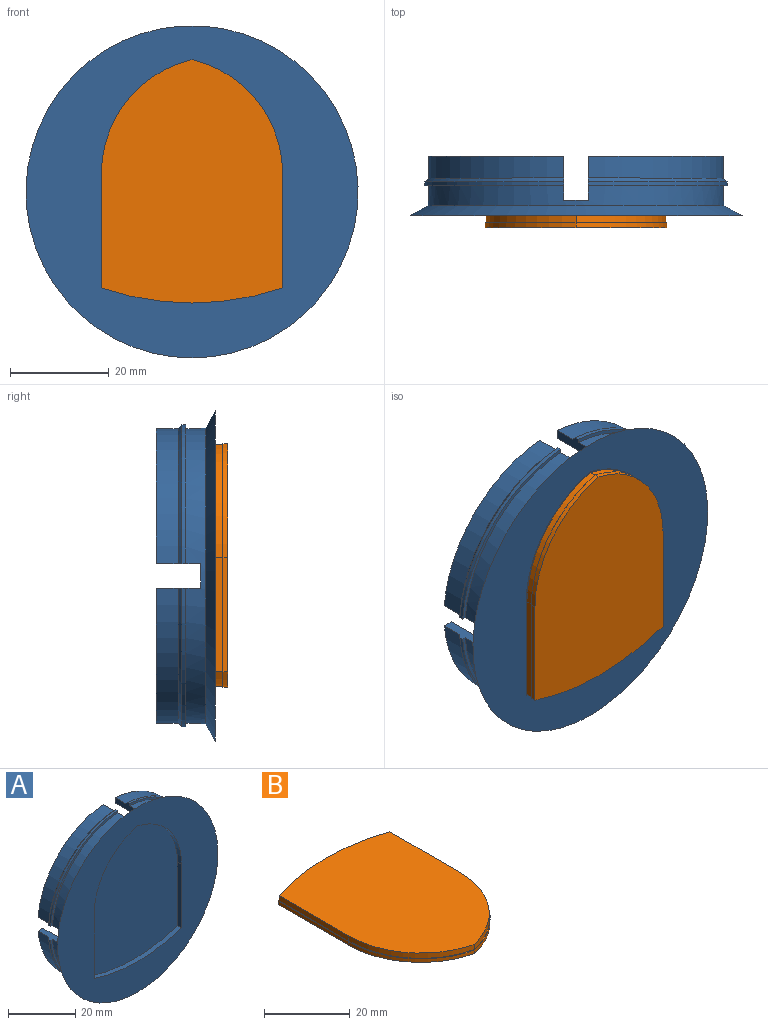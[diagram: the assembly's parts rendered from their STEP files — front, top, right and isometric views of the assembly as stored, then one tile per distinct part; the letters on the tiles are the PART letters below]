
ASSEMBLY  parts=2 mates=1
PART A: 42 faces, bbox 67.4x12x67.4 mm
  f0: plane 67.4x67.4mm, normal (0,-1,0), area 2005.3mm2, adj f35,f36,f37,f38,f39,f40
  f1: cylinder r=28mm len=25.39mm, axis (0,-1,0), area 350.8mm2, adj f12,f29,f31,f34
  f2: cylinder r=28mm len=25.39mm, axis (0,-1,0), area 350.8mm2, adj f14,f26,f28,f34
  f3: cylinder r=28mm len=25.39mm, axis (0,-1,0), area 350.8mm2, adj f13,f27,f32,f34
  f4: cylinder r=30mm len=60mm, axis (0,-1,0), area 700.1mm2, adj f8,f9,f10,f22,f26,f27,f28,f29
  f5: cylinder r=30.75mm len=28.15mm, axis (0,-1,0), area 34.6mm2, adj f8,f18,f27,f32
  f6: cylinder r=30.75mm len=28.15mm, axis (0,-1,0), area 34.6mm2, adj f9,f19,f30,f33
  f7: cylinder r=30.75mm len=28.15mm, axis (0,-1,0), area 34.6mm2, adj f10,f20,f26,f28
  f8: plane 28.15x28.15mm, normal (0,-1,0), area 32mm2, adj f4,f5,f27,f32
  f9: plane 28.15x28.15mm, normal (0,-1,0), area 32mm2, adj f4,f6,f30,f33
  f10: plane 28.15x28.15mm, normal (0,-1,0), area 32mm2, adj f4,f7,f26,f28
  f11: plane 27.4x27.4mm, normal (0,1,0), area 81.1mm2, adj f16,f24,f30,f33
  f12: plane 27.4x27.4mm, normal (0,1,0), area 81.1mm2, adj f1,f23,f29,f31
  f13: plane 27.4x27.4mm, normal (0,1,0), area 81.1mm2, adj f3,f15,f27,f32
  f14: plane 27.4x27.4mm, normal (0,1,0), area 81.1mm2, adj f2,f17,f26,f28
  f15: cylinder r=30mm len=27.4mm, axis (0,-1,0), area 187.4mm2, adj f13,f18,f27,f32
  f16: cylinder r=30mm len=27.4mm, axis (0,-1,0), area 187.4mm2, adj f11,f19,f30,f33
  f17: cylinder r=30mm len=27.4mm, axis (0,-1,0), area 187.4mm2, adj f14,f20,f26,f28
  f18: cone r=29.75mm half-angle=45deg, axis (0,-1,0), area 45.3mm2, adj f5,f15,f27,f32
  f19: cone r=29.75mm half-angle=45deg, axis (0,-1,0), area 45.3mm2, adj f6,f16,f30,f33
  f20: cone r=29.75mm half-angle=45deg, axis (0,-1,0), area 45.3mm2, adj f7,f17,f26,f28
  f21: cylinder r=30.75mm len=28.15mm, axis (0,-1,0), area 34.6mm2, adj f22,f25,f29,f31
  f22: plane 28.15x28.15mm, normal (0,-1,0), area 32mm2, adj f4,f21,f29,f31
  f23: cylinder r=30mm len=27.4mm, axis (0,-1,0), area 187.4mm2, adj f12,f25,f29,f31
  f24: cylinder r=28mm len=25.39mm, axis (0,-1,0), area 350.8mm2, adj f11,f30,f33,f34
  f25: cone r=29.75mm half-angle=45deg, axis (0,-1,0), area 45.3mm2, adj f21,f23,f29,f31
  f26: plane 9x2.76mm, normal (-1,0,0), area 19mm2, adj f2,f4,f7,f10,f14,f17,f20,f34
  f27: plane 9x2.76mm, normal (1,0,0), area 19mm2, adj f3,f4,f5,f8,f13,f15,f18,f34
  f28: plane 9x2.76mm, normal (0,0,-1), area 19mm2, adj f2,f4,f7,f10,f14,f17,f20,f34
  f29: plane 9x2.76mm, normal (0,0,1), area 19mm2, adj f1,f4,f12,f21,f22,f23,f25,f34
  f30: plane 9x2.76mm, normal (1,0,0), area 19mm2, adj f4,f6,f9,f11,f16,f19,f24,f34
  f31: plane 9x2.76mm, normal (-1,0,0), area 19mm2, adj f1,f4,f12,f21,f22,f23,f25,f34
  f32: plane 9x2.76mm, normal (0,0,-1), area 19mm2, adj f3,f4,f5,f8,f13,f15,f18,f34
  f33: plane 9x2.76mm, normal (0,0,1), area 19mm2, adj f4,f6,f9,f11,f16,f19,f24,f34
  f34: plane 60x60mm, normal (0,1,0), area 2503.1mm2, adj f1,f2,f3,f4,f24,f26,f27,f28
  f35: cone r=33.7mm half-angle=62deg, axis (0,-1,0), area 838.6mm2, adj f0,f4
  f36: cylinder r=56.91mm len=36.8mm, axis (0,-1,0), area 63.7mm2, adj f0,f37,f40,f41
  f37: plane 23.14x1.7mm, normal (-1,0,0), area 39.3mm2, adj f0,f36,f38,f41
  f38: cylinder r=23.83mm len=23.21mm, axis (0,-1,0), area 54.3mm2, adj f0,f37,f39,f41
  f39: cylinder r=23.83mm len=23.21mm, axis (0,-1,0), area 54.3mm2, adj f0,f38,f40,f41
  f40: plane 23.14x1.7mm, normal (1,0,0), area 39.3mm2, adj f0,f36,f39,f41
  f41: plane 49.41x36.8mm, normal (0,-1,0), area 1562.6mm2, adj f36,f37,f38,f39,f40
PART B: 13 faces, bbox 36.8x49.4x2.5 mm
  f0: plane 23x1.5mm, normal (1,0,0), area 34.5mm2, adj f1,f4,f5,f11
  f1: cylinder r=56.71mm len=36.4mm, axis (0,0,-1), area 55.6mm2, adj f0,f2,f5,f11
  f2: plane 23x1.5mm, normal (-1,0,0), area 34.5mm2, adj f1,f3,f5,f11
  f3: cylinder r=23.63mm len=23mm, axis (0,0,-1), area 47.5mm2, adj f2,f4,f5,f11
  f4: cylinder r=23.63mm len=23mm, axis (0,0,-1), area 47.5mm2, adj f0,f3,f5,f11
  f5: plane 49x36.4mm, normal (0,0,1), area 1533.2mm2, adj f0,f1,f2,f3,f4
  f6: cylinder r=56.91mm len=36.8mm, axis (0,0,-1), area 37.5mm2, adj f7,f10,f11,f12
  f7: plane 23.14x1mm, normal (-1,0,0), area 23.1mm2, adj f6,f8,f11,f12
  f8: cylinder r=23.83mm len=23.21mm, axis (0,0,-1), area 32mm2, adj f7,f9,f11,f12
  f9: cylinder r=23.83mm len=23.21mm, axis (0,0,-1), area 32mm2, adj f8,f10,f11,f12
  f10: plane 23.14x1mm, normal (1,0,0), area 23.1mm2, adj f6,f9,f11,f12
  f11: plane 49.41x36.8mm, normal (0,0,1), area 29.4mm2, adj f0,f1,f2,f3,f4,f6,f7,f8
  f12: plane 49.41x36.8mm, normal (0,0,-1), area 1562.6mm2, adj f6,f7,f8,f9,f10
PLACE A t=(25.68,34.51,37)mm
PLACE B rot(axis=(-1,0,0),90deg) t=(25.68,32.01,40.64)mm
MATE fastened B.f5 <-> A.f35  axis (0,1,0) through (25.68,34.51,37)mm
